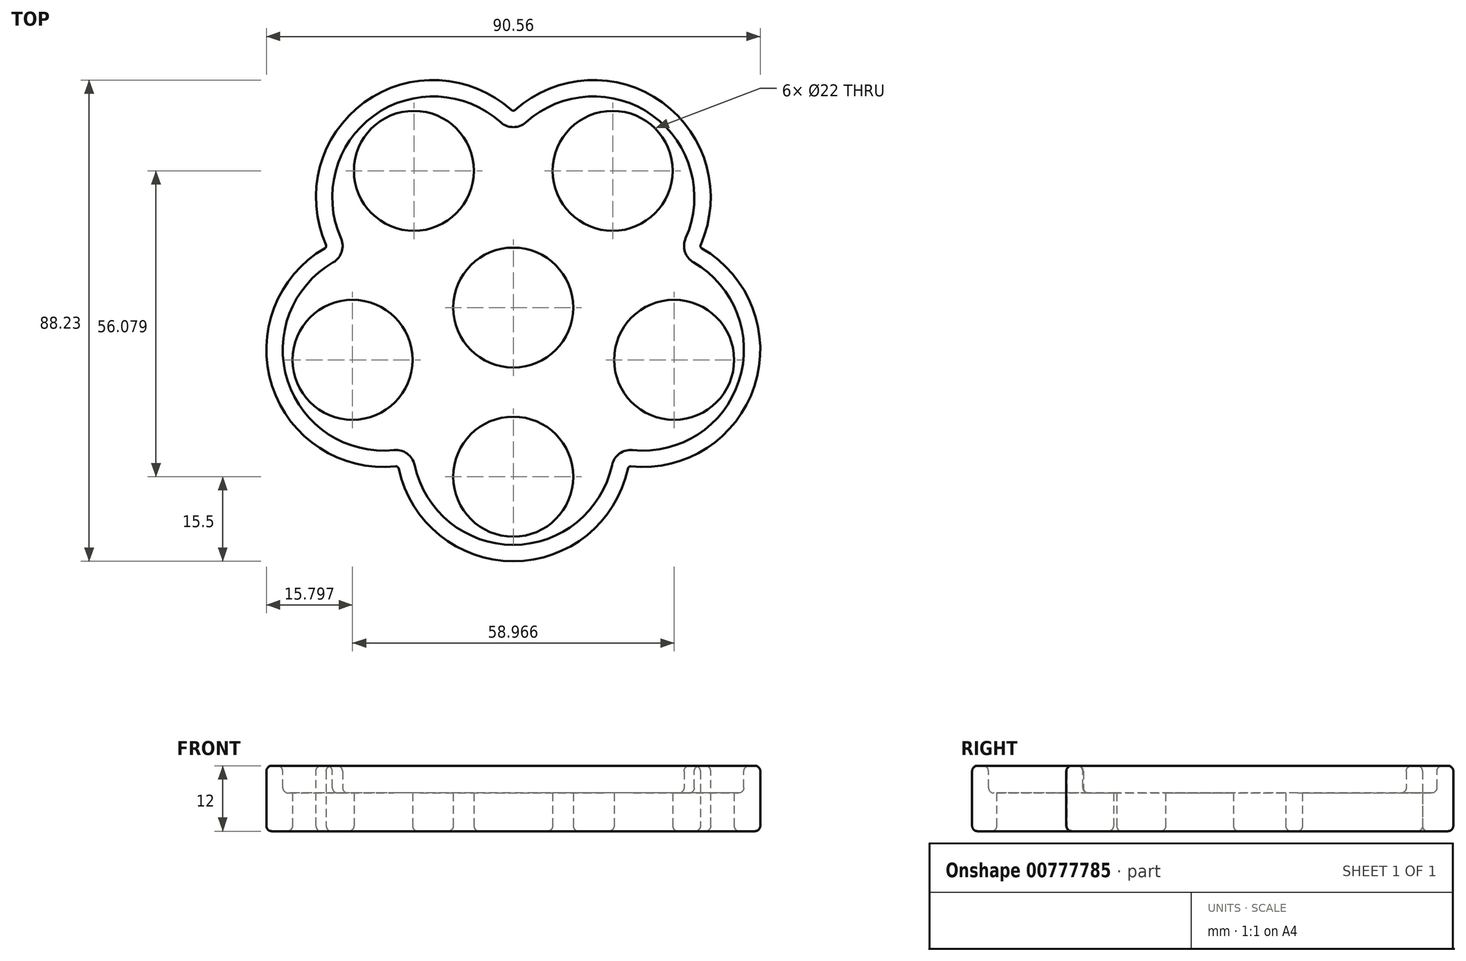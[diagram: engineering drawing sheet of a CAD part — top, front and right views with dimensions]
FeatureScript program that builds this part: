
annotation { "Feature Type Name" : "Feature", "Feature Type Description" : "" }
export const myFeature = defineFeature(function(context is Context, id is Id, definition is map)
    precondition{}
    {
        {
            var Q0;
            Q0=qCreatedBy(makeId("Top.planeOp"),FACE);
            var sketch = newSketch(context, id + "F0", { "sketchPlane" : qUnion([Q0])});
            skCircle(sketch, "E0.cCircle", {"center": v(0, 0) * mm, "radius": 25 * mm, "construction": true});
            skPoint(sketch, "E0.0.midPoint", {"position": v(14.7, 20.23) * mm});
            skArc(sketch, "E1", {"start": v(0, 33.8) * mm, "mid": v(-26.45, 36.4) * mm, "end": v(-32.14, 10.44) * mm});
            skArc(sketch, "E2", {"start": v(32.14, 10.44) * mm, "mid": v(26.45, 36.4) * mm, "end": v(0, 33.8) * mm});
            skArc(sketch, "E3", {"start": v(19.86, -27.34) * mm, "mid": v(42.8, -13.9) * mm, "end": v(32.14, 10.44) * mm});
            skArc(sketch, "E4", {"start": v(-19.86, -27.34) * mm, "mid": v(0, -45) * mm, "end": v(19.86, -27.34) * mm});
            skArc(sketch, "E5", {"start": v(-32.14, 10.44) * mm, "mid": v(-42.8, -13.9) * mm, "end": v(-19.86, -27.34) * mm});
            skCircle(sketch, "E6", {"center": v(0, 0) * mm, "radius": 33.8 * mm, "construction": true});
            skCircle(sketch, "E7", {"center": v(0, 0) * mm, "radius": 11 * mm});
            skCircle(sketch, "E8", {"center": v(-18.22, 25.08) * mm, "radius": 11 * mm});
            skCircle(sketch, "E9", {"center": v(18.22, 25.08) * mm, "radius": 11 * mm});
            skCircle(sketch, "E10", {"center": v(29.48, -9.58) * mm, "radius": 11 * mm});
            skCircle(sketch, "E11", {"center": v(0, -31) * mm, "radius": 11 * mm});
            skCircle(sketch, "E12", {"center": v(-29.48, -9.58) * mm, "radius": 11 * mm});
            skCircle(sketch, "E13", {"center": v(0, 0) * mm, "radius": 31 * mm, "construction": true});
            skLineSegment(sketch, "E14", {"start": v(0, 0) * mm, "end": v(0, 61.86) * mm, "construction": true});
            skLineSegment(sketch, "E15", {"start": v(0, 0) * mm, "end": v(38.47, 52.95) * mm, "construction": true});
            skLineSegment(sketch, "E16", {"start": v(0, 0) * mm, "end": v(76, -24.7) * mm, "construction": true});
            skLineSegment(sketch, "E17", {"start": v(0, 0) * mm, "end": v(0, -42) * mm, "construction": true});
            skLineSegment(sketch, "E18", {"start": v(0, 0) * mm, "end": v(-67.56, -21.95) * mm, "construction": true});
            skLineSegment(sketch, "E19", {"start": v(0, 0) * mm, "end": v(-35.13, 48.35) * mm, "construction": true});
            skSolve(sketch);
        }
        {
            var Q0;
            Q0=qSketchRegion(id+"F0",true);
            extrude(context, id + "F1", {"entities" : qUnion([Q0]), "depth" : 7 * mm, "offsetDistance" : 25.4 * mm});
        }
        {
            var Q0;
            Q0=makeQuery(id+"F1.opExtrude","SWEPT_EDGE",EDGE,{"disambiguationData":[OSD([sQuery(id+"F0.wireOp",EDGE,"E3"),sQuery(id+"F0.wireOp",EDGE,"E4")])]});
            var Q1;
            Q1=makeQuery(id+"F1.opExtrude","SWEPT_EDGE",EDGE,{"disambiguationData":[OSD([sQuery(id+"F0.wireOp",EDGE,"E2"),sQuery(id+"F0.wireOp",EDGE,"E3")])]});
            var Q2;
            Q2=makeQuery(id+"F1.opExtrude","SWEPT_EDGE",EDGE,{"disambiguationData":[OSD([sQuery(id+"F0.wireOp",EDGE,"E1"),sQuery(id+"F0.wireOp",EDGE,"E2")])]});
            var Q3;
            Q3=makeQuery(id+"F1.opExtrude","SWEPT_EDGE",EDGE,{"disambiguationData":[OSD([sQuery(id+"F0.wireOp",EDGE,"E1"),sQuery(id+"F0.wireOp",EDGE,"E5")])]});
            var Q4;
            Q4=makeQuery(id+"F1.opExtrude","SWEPT_EDGE",EDGE,{"disambiguationData":[OSD([sQuery(id+"F0.wireOp",EDGE,"E4"),sQuery(id+"F0.wireOp",EDGE,"E5")])]});
            fillet(context, id + "F2", {"entities" : qUnion([Q0, Q1, Q2, Q3, Q4]), "radius" : 2 * mm, "tangentPropagation" : true, "allowEdgeOverflow" : false});
        }
        {
            var Q0;
            Q0=qCreatedBy(makeId("Right.planeOp"),FACE);
            var sketch = newSketch(context, id + "F3", { "sketchPlane" : qUnion([Q0])});
            skLineSegment(sketch, "E20.bottom", {"start": v(-46.5, 12) * mm, "end": v(-43.5, 12) * mm});
            skLineSegment(sketch, "E20.top", {"start": v(-46.5, 0) * mm, "end": v(-43.5, 0) * mm});
            skLineSegment(sketch, "E20.left", {"start": v(-46.5, 12) * mm, "end": v(-46.5, 0) * mm});
            skLineSegment(sketch, "E20.right", {"start": v(-43.5, 12) * mm, "end": v(-43.5, 0) * mm});
            skSolve(sketch);
        }
        {
            var Q0;
            Q0 = qSketchRegion(id + "F3", true);
            var Q1;
            Q1=makeQuery(id+"F1.opExtrude","CAP_EDGE",EDGE,{"disambiguationData":[OSD([sQuery(id+"F0.wireOp",EDGE,"E4")])],"isStart":false});
            var Q2;
            Q2=makeQuery(id+"F1.opExtrude","CAP_EDGE",EDGE,{"disambiguationData":[OSD([sQuery(id+"F0.wireOp",EDGE,"E5")])],"isStart":false});
            var Q3;
            {var subQ0=sQuery(id+"F0.wireOp",EDGE,"E5");var subQ1=sQuery(id+"F0.wireOp",EDGE,"E4");Q3=makeQuery(id+"F2.opFillet","BLEND_EDGE",EDGE,{"blendedFrom":[makeQuery(id+"F1.opExtrude","SWEPT_EDGE",EDGE,{"disambiguationData":[OSD([subQ1,subQ0])]}),makeQuery(id+"F1.opExtrude","CAP_FACE",FACE,{"disambiguationData":[OSD([sQuery(id+"F0.wireOp",EDGE,"E1"),sQuery(id+"F0.wireOp",EDGE,"E2"),sQuery(id+"F0.wireOp",EDGE,"E3"),subQ1,subQ0,sQuery(id+"F0.wireOp",EDGE,"E7"),sQuery(id+"F0.wireOp",EDGE,"E8"),sQuery(id+"F0.wireOp",EDGE,"E9"),sQuery(id+"F0.wireOp",EDGE,"E10"),sQuery(id+"F0.wireOp",EDGE,"E11"),sQuery(id+"F0.wireOp",EDGE,"E12")])],"isStart":false})],"blendedInto":[makeQuery(id+"F1.opExtrude","CAP_FACE",FACE,{"disambiguationData":[OSD([sQuery(id+"F0.wireOp",EDGE,"E1"),sQuery(id+"F0.wireOp",EDGE,"E2"),sQuery(id+"F0.wireOp",EDGE,"E3"),subQ1,subQ0,sQuery(id+"F0.wireOp",EDGE,"E7"),sQuery(id+"F0.wireOp",EDGE,"E8"),sQuery(id+"F0.wireOp",EDGE,"E9"),sQuery(id+"F0.wireOp",EDGE,"E10"),sQuery(id+"F0.wireOp",EDGE,"E11"),sQuery(id+"F0.wireOp",EDGE,"E12")])],"isStart":false})]});}
            var Q4;
            {var subQ0=sQuery(id+"F0.wireOp",EDGE,"E5");var subQ1=sQuery(id+"F0.wireOp",EDGE,"E1");Q4=makeQuery(id+"F2.opFillet","BLEND_EDGE",EDGE,{"blendedFrom":[makeQuery(id+"F1.opExtrude","SWEPT_EDGE",EDGE,{"disambiguationData":[OSD([subQ1,subQ0])]}),makeQuery(id+"F1.opExtrude","CAP_FACE",FACE,{"disambiguationData":[OSD([subQ1,sQuery(id+"F0.wireOp",EDGE,"E2"),sQuery(id+"F0.wireOp",EDGE,"E3"),sQuery(id+"F0.wireOp",EDGE,"E4"),subQ0,sQuery(id+"F0.wireOp",EDGE,"E7"),sQuery(id+"F0.wireOp",EDGE,"E8"),sQuery(id+"F0.wireOp",EDGE,"E9"),sQuery(id+"F0.wireOp",EDGE,"E10"),sQuery(id+"F0.wireOp",EDGE,"E11"),sQuery(id+"F0.wireOp",EDGE,"E12")])],"isStart":false})],"blendedInto":[makeQuery(id+"F1.opExtrude","CAP_FACE",FACE,{"disambiguationData":[OSD([subQ1,sQuery(id+"F0.wireOp",EDGE,"E2"),sQuery(id+"F0.wireOp",EDGE,"E3"),sQuery(id+"F0.wireOp",EDGE,"E4"),subQ0,sQuery(id+"F0.wireOp",EDGE,"E7"),sQuery(id+"F0.wireOp",EDGE,"E8"),sQuery(id+"F0.wireOp",EDGE,"E9"),sQuery(id+"F0.wireOp",EDGE,"E10"),sQuery(id+"F0.wireOp",EDGE,"E11"),sQuery(id+"F0.wireOp",EDGE,"E12")])],"isStart":false})]});}
            var Q5;
            Q5=makeQuery(id+"F1.opExtrude","CAP_EDGE",EDGE,{"disambiguationData":[OSD([sQuery(id+"F0.wireOp",EDGE,"E1")])],"isStart":false});
            var Q6;
            {var subQ0=sQuery(id+"F0.wireOp",EDGE,"E2");var subQ1=sQuery(id+"F0.wireOp",EDGE,"E1");Q6=makeQuery(id+"F2.opFillet","BLEND_EDGE",EDGE,{"blendedFrom":[makeQuery(id+"F1.opExtrude","SWEPT_EDGE",EDGE,{"disambiguationData":[OSD([subQ1,subQ0])]}),makeQuery(id+"F1.opExtrude","CAP_FACE",FACE,{"disambiguationData":[OSD([subQ1,subQ0,sQuery(id+"F0.wireOp",EDGE,"E3"),sQuery(id+"F0.wireOp",EDGE,"E4"),sQuery(id+"F0.wireOp",EDGE,"E5"),sQuery(id+"F0.wireOp",EDGE,"E7"),sQuery(id+"F0.wireOp",EDGE,"E8"),sQuery(id+"F0.wireOp",EDGE,"E9"),sQuery(id+"F0.wireOp",EDGE,"E10"),sQuery(id+"F0.wireOp",EDGE,"E11"),sQuery(id+"F0.wireOp",EDGE,"E12")])],"isStart":false})],"blendedInto":[makeQuery(id+"F1.opExtrude","CAP_FACE",FACE,{"disambiguationData":[OSD([subQ1,subQ0,sQuery(id+"F0.wireOp",EDGE,"E3"),sQuery(id+"F0.wireOp",EDGE,"E4"),sQuery(id+"F0.wireOp",EDGE,"E5"),sQuery(id+"F0.wireOp",EDGE,"E7"),sQuery(id+"F0.wireOp",EDGE,"E8"),sQuery(id+"F0.wireOp",EDGE,"E9"),sQuery(id+"F0.wireOp",EDGE,"E10"),sQuery(id+"F0.wireOp",EDGE,"E11"),sQuery(id+"F0.wireOp",EDGE,"E12")])],"isStart":false})]});}
            var Q7;
            Q7=makeQuery(id+"F1.opExtrude","CAP_EDGE",EDGE,{"disambiguationData":[OSD([sQuery(id+"F0.wireOp",EDGE,"E2")])],"isStart":false});
            var Q8;
            {var subQ0=sQuery(id+"F0.wireOp",EDGE,"E3");var subQ1=sQuery(id+"F0.wireOp",EDGE,"E2");Q8=makeQuery(id+"F2.opFillet","BLEND_EDGE",EDGE,{"blendedFrom":[makeQuery(id+"F1.opExtrude","SWEPT_EDGE",EDGE,{"disambiguationData":[OSD([subQ1,subQ0])]}),makeQuery(id+"F1.opExtrude","CAP_FACE",FACE,{"disambiguationData":[OSD([sQuery(id+"F0.wireOp",EDGE,"E1"),subQ1,subQ0,sQuery(id+"F0.wireOp",EDGE,"E4"),sQuery(id+"F0.wireOp",EDGE,"E5"),sQuery(id+"F0.wireOp",EDGE,"E7"),sQuery(id+"F0.wireOp",EDGE,"E8"),sQuery(id+"F0.wireOp",EDGE,"E9"),sQuery(id+"F0.wireOp",EDGE,"E10"),sQuery(id+"F0.wireOp",EDGE,"E11"),sQuery(id+"F0.wireOp",EDGE,"E12")])],"isStart":false})],"blendedInto":[makeQuery(id+"F1.opExtrude","CAP_FACE",FACE,{"disambiguationData":[OSD([sQuery(id+"F0.wireOp",EDGE,"E1"),subQ1,subQ0,sQuery(id+"F0.wireOp",EDGE,"E4"),sQuery(id+"F0.wireOp",EDGE,"E5"),sQuery(id+"F0.wireOp",EDGE,"E7"),sQuery(id+"F0.wireOp",EDGE,"E8"),sQuery(id+"F0.wireOp",EDGE,"E9"),sQuery(id+"F0.wireOp",EDGE,"E10"),sQuery(id+"F0.wireOp",EDGE,"E11"),sQuery(id+"F0.wireOp",EDGE,"E12")])],"isStart":false})]});}
            var Q9;
            Q9=makeQuery(id+"F1.opExtrude","CAP_EDGE",EDGE,{"disambiguationData":[OSD([sQuery(id+"F0.wireOp",EDGE,"E3")])],"isStart":false});
            var Q10;
            {var subQ0=sQuery(id+"F0.wireOp",EDGE,"E4");var subQ1=sQuery(id+"F0.wireOp",EDGE,"E3");Q10=makeQuery(id+"F2.opFillet","BLEND_EDGE",EDGE,{"blendedFrom":[makeQuery(id+"F1.opExtrude","SWEPT_EDGE",EDGE,{"disambiguationData":[OSD([subQ1,subQ0])]}),makeQuery(id+"F1.opExtrude","CAP_FACE",FACE,{"disambiguationData":[OSD([sQuery(id+"F0.wireOp",EDGE,"E1"),sQuery(id+"F0.wireOp",EDGE,"E2"),subQ1,subQ0,sQuery(id+"F0.wireOp",EDGE,"E5"),sQuery(id+"F0.wireOp",EDGE,"E7"),sQuery(id+"F0.wireOp",EDGE,"E8"),sQuery(id+"F0.wireOp",EDGE,"E9"),sQuery(id+"F0.wireOp",EDGE,"E10"),sQuery(id+"F0.wireOp",EDGE,"E11"),sQuery(id+"F0.wireOp",EDGE,"E12")])],"isStart":false})],"blendedInto":[makeQuery(id+"F1.opExtrude","CAP_FACE",FACE,{"disambiguationData":[OSD([sQuery(id+"F0.wireOp",EDGE,"E1"),sQuery(id+"F0.wireOp",EDGE,"E2"),subQ1,subQ0,sQuery(id+"F0.wireOp",EDGE,"E5"),sQuery(id+"F0.wireOp",EDGE,"E7"),sQuery(id+"F0.wireOp",EDGE,"E8"),sQuery(id+"F0.wireOp",EDGE,"E9"),sQuery(id+"F0.wireOp",EDGE,"E10"),sQuery(id+"F0.wireOp",EDGE,"E11"),sQuery(id+"F0.wireOp",EDGE,"E12")])],"isStart":false})]});}
            sweep(context, id + "F4", {"operationType" : NewBodyOperationType.ADD, "profiles" : qUnion([Q0]), "path" : qUnion([Q1, Q2, Q3, Q4, Q5, Q6, Q7, Q8, Q9, Q10])});
        }
        {
            var Q0;
            Q0=makeQuery(id+"F4.opSweep","SWEPT_FACE",FACE,{"disambiguationData":[OSD([sQuery(id+"F0.wireOp",EDGE,"E4"),sQuery(id+"F3.wireOp",EDGE,"E20.bottom")])]});
            var Q1;
            Q1=makeQuery(id+"F4.opSweep","SWEPT_FACE",FACE,{"disambiguationData":[OSD([sQuery(id+"F0.wireOp",EDGE,"E4"),sQuery(id+"F3.wireOp",EDGE,"E20.top")])]});
            fillet(context, id + "F5", {"entities" : qUnion([Q0, Q1]), "radius" : 1 * mm, "tangentPropagation" : true, "allowEdgeOverflow" : false});
        }
        {
            var Q0;
            {var subQ0=sQuery(id+"F0.wireOp",EDGE,"E3");Q0=makeQuery(id+"F4.boolean.opBoolean","INTERSECT",EDGE,{"derivedFrom":[makeQuery(id+"F1.opExtrude","CAP_FACE",FACE,{"disambiguationData":[OSD([sQuery(id+"F0.wireOp",EDGE,"E1"),sQuery(id+"F0.wireOp",EDGE,"E2"),subQ0,sQuery(id+"F0.wireOp",EDGE,"E4"),sQuery(id+"F0.wireOp",EDGE,"E5"),sQuery(id+"F0.wireOp",EDGE,"E7"),sQuery(id+"F0.wireOp",EDGE,"E8"),sQuery(id+"F0.wireOp",EDGE,"E9"),sQuery(id+"F0.wireOp",EDGE,"E10"),sQuery(id+"F0.wireOp",EDGE,"E11"),sQuery(id+"F0.wireOp",EDGE,"E12")])],"isStart":true}),makeQuery(id+"F4.opSweep","SWEPT_FACE",FACE,{"disambiguationData":[OSD([subQ0,sQuery(id+"F3.wireOp",EDGE,"E20.right")])]})]});}
            var Q1;
            {var subQ0=sQuery(id+"F0.wireOp",EDGE,"E4");Q1=makeQuery(id+"F4.boolean.opBoolean","INTERSECT",EDGE,{"derivedFrom":[makeQuery(id+"F1.opExtrude","CAP_FACE",FACE,{"disambiguationData":[OSD([sQuery(id+"F0.wireOp",EDGE,"E1"),sQuery(id+"F0.wireOp",EDGE,"E2"),sQuery(id+"F0.wireOp",EDGE,"E3"),subQ0,sQuery(id+"F0.wireOp",EDGE,"E5"),sQuery(id+"F0.wireOp",EDGE,"E7"),sQuery(id+"F0.wireOp",EDGE,"E8"),sQuery(id+"F0.wireOp",EDGE,"E9"),sQuery(id+"F0.wireOp",EDGE,"E10"),sQuery(id+"F0.wireOp",EDGE,"E11"),sQuery(id+"F0.wireOp",EDGE,"E12")])],"isStart":false}),makeQuery(id+"F4.opSweep","SWEPT_FACE",FACE,{"disambiguationData":[OSD([subQ0,sQuery(id+"F3.wireOp",EDGE,"E20.right")])]})]});}
            fillet(context, id + "F6", {"entities" : qUnion([Q0, Q1]), "radius" : 1 * mm, "tangentPropagation" : true, "allowEdgeOverflow" : false});
        }
    });
